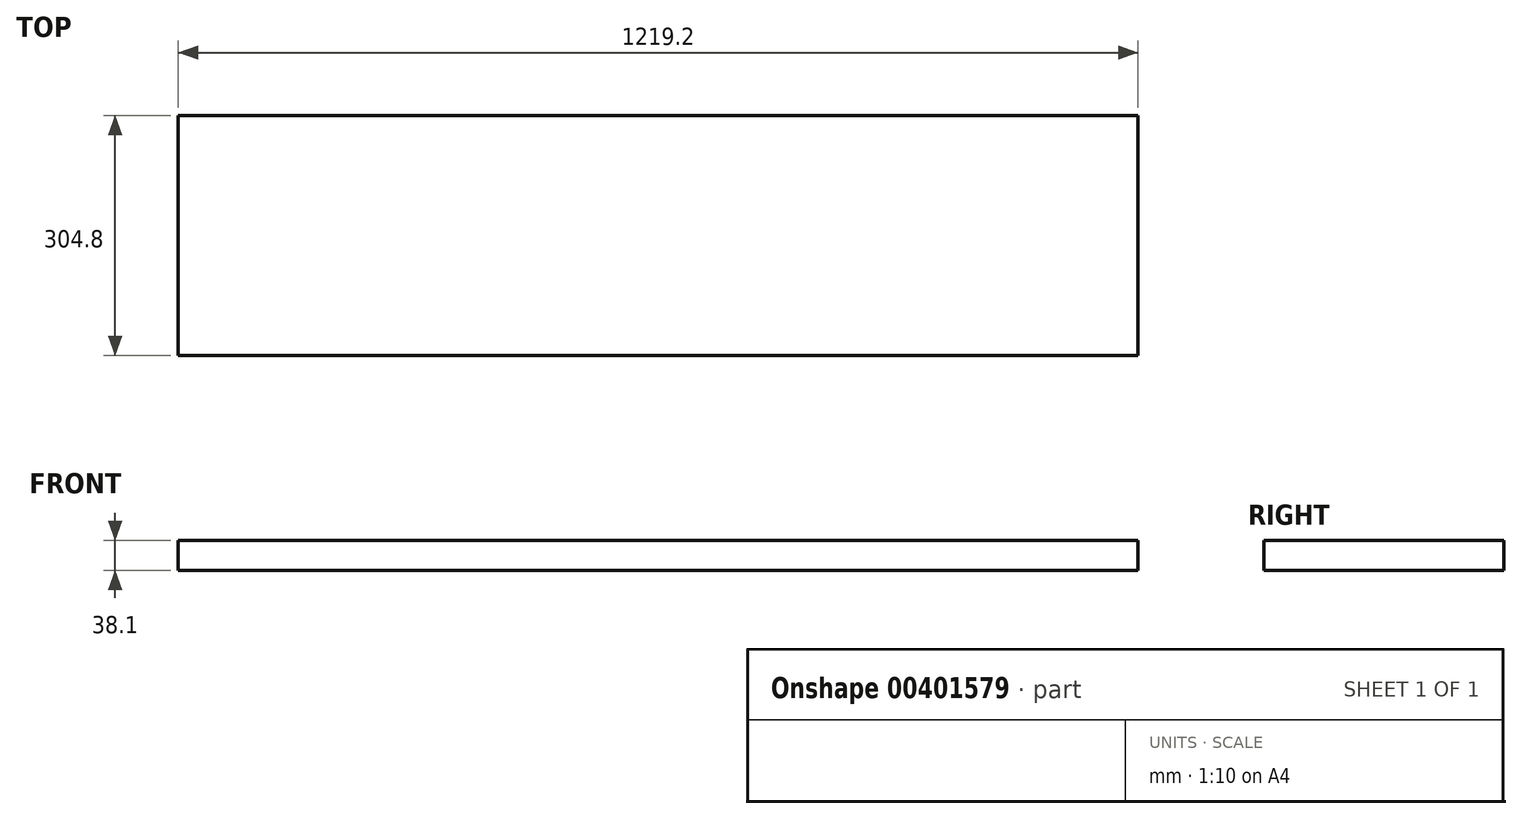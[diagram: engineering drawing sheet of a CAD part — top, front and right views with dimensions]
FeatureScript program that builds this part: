
annotation { "Feature Type Name" : "Feature", "Feature Type Description" : "" }
export const myFeature = defineFeature(function(context is Context, id is Id, definition is map)
    precondition{}
    {
        {
            var Q0;
            Q0=qCreatedBy(makeId("Front.planeOp"),FACE);
            var sketch = newSketch(context, id + "F0", { "sketchPlane" : qUnion([Q0])});
            skLineSegment(sketch, "E0.bottom", {"start": v(609.6, 182.98) * mm, "end": v(-609.6, 182.98) * mm});
            skLineSegment(sketch, "E0.top", {"start": v(609.6, 144.88) * mm, "end": v(-609.6, 144.88) * mm});
            skLineSegment(sketch, "E0.left", {"start": v(609.6, 182.98) * mm, "end": v(609.6, 144.88) * mm});
            skLineSegment(sketch, "E0.right", {"start": v(-609.6, 182.98) * mm, "end": v(-609.6, 144.88) * mm});
            skPoint(sketch, "E0.middle", {"position": v(0, 163.93) * mm});
            skSolve(sketch);
        }
        {
            var Q0;
            Q0=makeQuery(id+"F0.imprint","IMPRINT",FACE,{"disambiguationData":[TD([[makeQuery(id+"F0.imprint","IMPRINT",EDGE,{"derivedFrom":sQuery(id+"F0.wireOp",EDGE,"E0.bottom")}),1.0]])]});
            extrude(context, id + "F1", {"entities" : qUnion([Q0]), "oppositeDirection" : true, "depth" : 304.8 * mm});
        }
    });
